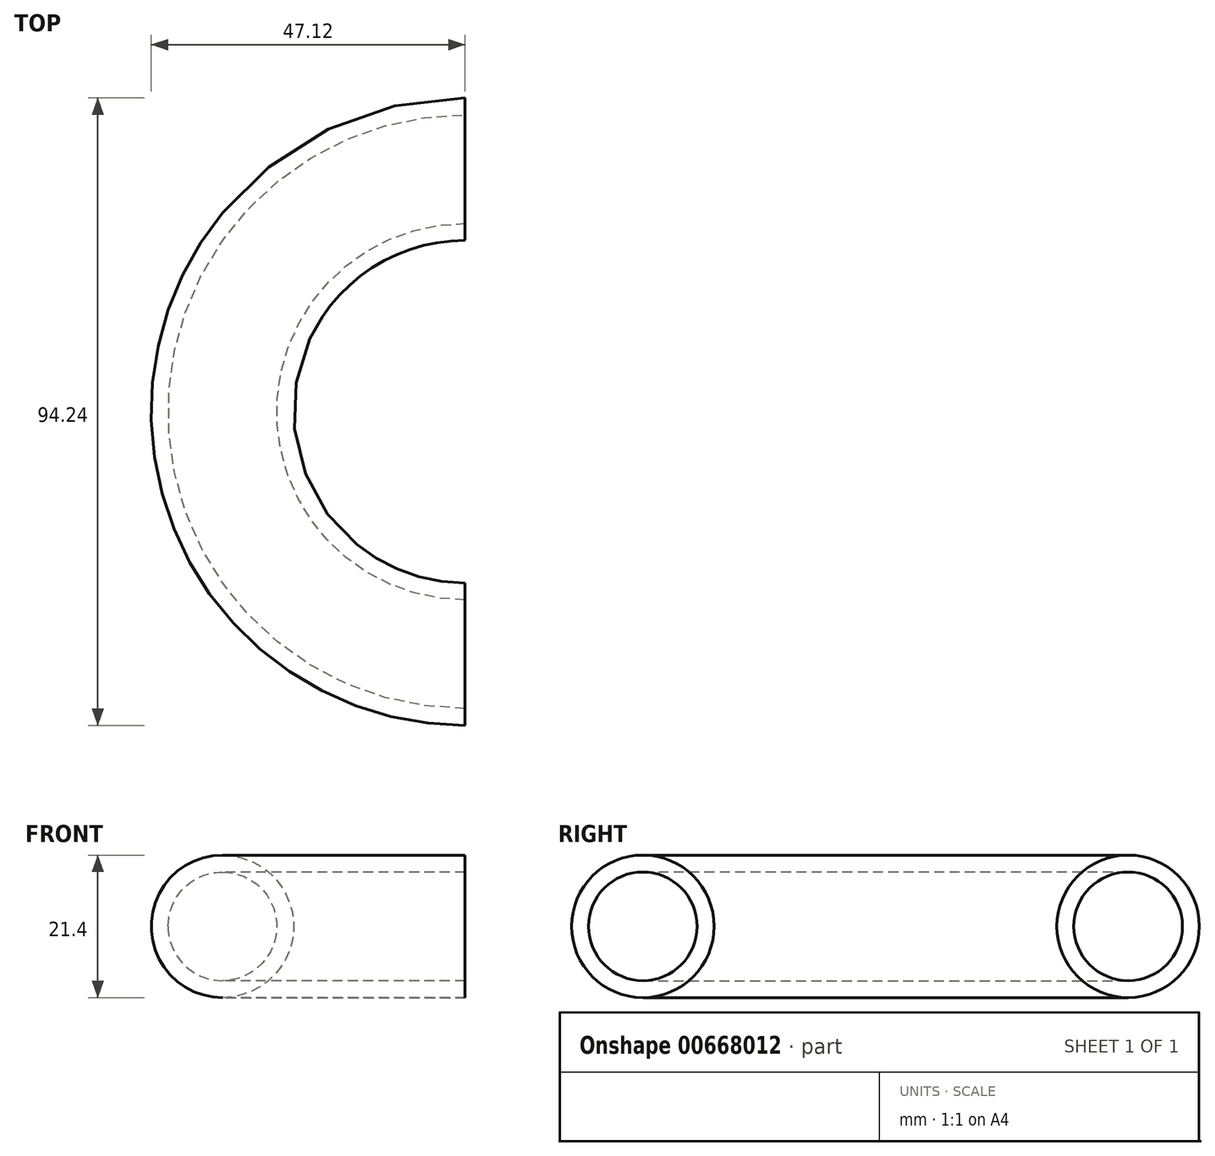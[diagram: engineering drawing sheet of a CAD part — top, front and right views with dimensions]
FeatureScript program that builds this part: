
annotation { "Feature Type Name" : "Feature", "Feature Type Description" : "" }
export const myFeature = defineFeature(function(context is Context, id is Id, definition is map)
    precondition{}
    {
        {
            var Q0;
            Q0=qCreatedBy(makeId("Right.planeOp"),FACE);
            var sketch = newSketch(context, id + "F0", { "sketchPlane" : qUnion([Q0])});
            skCircle(sketch, "E0", {"center": v(36.43, 0) * mm, "radius": 10.7 * mm});
            skLineSegment(sketch, "E1", {"start": v(0, -8.59) * mm, "end": v(0, 8.07) * mm});
            skSolve(sketch);
        }
        {
            var Q0;
            Q0=makeQuery(id+"F0.imprint","IMPRINT",FACE,{"disambiguationData":[TD([[makeQuery(id+"F0.imprint","IMPRINT",EDGE,{"derivedFrom":sQuery(id+"F0.wireOp",EDGE,"E0")}),1.0]])]});
            var Q1;
            Q1=sQuery(id+"F0.wireOp",EDGE,"E1");
            revolve(context, id + "F1", {"entities" : qUnion([Q0]), "axis" : qUnion([Q1]), "revolveType" : RevolveType.ONE_DIRECTION, "angle" : 180 * degree});
        }
        {
            var Q0;
            Q0=makeQuery(id+"F1.opRevolve","CAP_FACE",FACE,{"disambiguationData":[OSD([sQuery(id+"F0.wireOp",EDGE,"E0")])],"isStart":false});
            var Q1;
            Q1=makeQuery(id+"F1.opRevolve","CAP_FACE",FACE,{"disambiguationData":[OSD([sQuery(id+"F0.wireOp",EDGE,"E0")])],"isStart":true});
            shell(context, id + "F2", {"entities" : qUnion([Q0, Q1]), "thickness" : 2.54 * mm});
        }
    });
